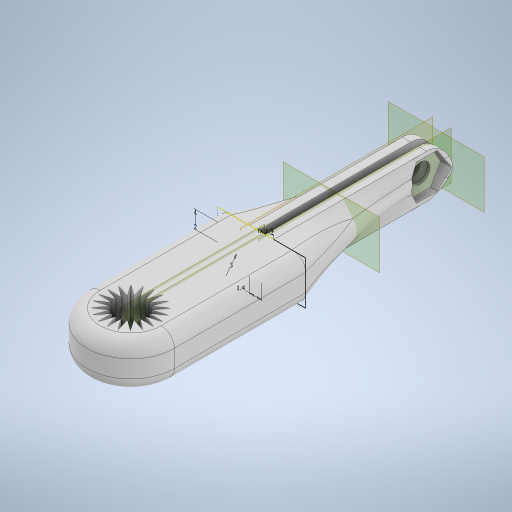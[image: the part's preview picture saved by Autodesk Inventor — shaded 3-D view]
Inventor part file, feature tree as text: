
AUTODESK INVENTOR PART (.ipt)
format: ipt  version: 2023.1 (Build 271208000, 208)  size: 648,704 bytes
history: native  units: mm
features: extrude x8, plane x7, sketch x7, projected_geometry x6, other x4, loft x2, fillet x2
ambient origin geometry x8: Origin, YZ Plane, XZ Plane, XY Plane, X Axis, Y Axis, Z Axis, Center Point
bodies: Solid1 (feature_tree)
feature tree (36):
  extrude  "Horn Base"  Depth=20.0mm
  extrude  "Servo Spline Cut"  Depth=2.0mm TaperAngle=0.0deg
  plane  "Work Plane (Clip Axis)"
  sketch  "Sketch5"  dims[d0=10.0mm d1=20.0mm]
  plane  "Work Plane2"
  sketch  "Sketch6"  dims[d2=3.0mm d3=2.0mm d4=0.0mm]
  plane  "Work Plane3"
  sketch  "Sketch7"  dims[d5=3.4mm d6=1.5mm]
  plane  "Work Plane4"
  sketch  "Sketch8"  dims[d7=3.141593mm d9=200.0mm d11=360.0deg]
  extrude  "Extrusion3"  Depth=1.5mm
  plane  "Work Plane5"
  extrude  "Extrusion4"  Depth=200.0mm TaperAngle=360.0deg
  loft  "Loft4"
  loft  "Loft5"
  fillet  "Fillet4"  Radius=3.0mm
  fillet  "Fillet5"  [1 undecoded]
  plane  "Work Plane6"
  sketch  "Sketch10"  dims[d23=1.4mm d24=2.0mm d25=3.0mm d26=-4.6mm]
  extrude  "Extrusion5"  Depth=20.0mm
  extrude  "Extrusion6"  Depth=8.0mm
  plane  "Work Plane7"
  sketch  "Sketch11"  dims[d27=20.0mm d28=20.0mm d31=8.0mm d32=1.4mm d33=2.0mm d34=1.5mm d35=2.0mm d36=1.4mm d37=0.5mm d38=1.0mm d39=4.0mm d46=1.0mm d47=0.0mm d62=1.4mm d63=-0.8mm d64=1.0mm d65=0.0mm d66=0.0mm d67=90.0deg d68=0.0mm d69=90.0deg d70=0.0mm d71=90.0deg d72=0.0mm d73=90.0deg d74=0.0mm d75=90.0deg d76=0.0mm d77=90.0deg d78=1.5mm d79=2.5mm d80=-1.0mm d81=2.15mm d82=1.0mm d83=45.0deg d84=1.0mm d85=0.0mm d86=-0.3mm d87=2.35mm d88=1.0mm d89=2.0mm d90=0.0mm d91=0.0mm d92=2.0mm d93=0.0mm d60=0.0mm d61=0.0mm]
  extrude  "Extrusion7"  Depth=1.4mm
  extrude  "Extrusion8"  Depth=2.0mm
  other  "Horn Base Profile"
  other  "Spline Profile"
  sketch  "Sketch9"  dims[d13=3.0mm d14=0.0mm d15=-2.5mm]
  other  "Edges3"
  other  "Edges4"
  projected_geometry  "Project Cut Edges1"
  projected_geometry  "Project Cut Edges2"
  projected_geometry  "Project Cut Edges3"
  projected_geometry  "Project Cut Edges4"
  projected_geometry  "Project Cut Edges5"
  projected_geometry  "Project Cut Edges6"
note: 1 required parameter value undecoded (feature->parameter linkage not recoverable at this tier; creation-order binding heuristic only, values carry confidence <= 0.55)
